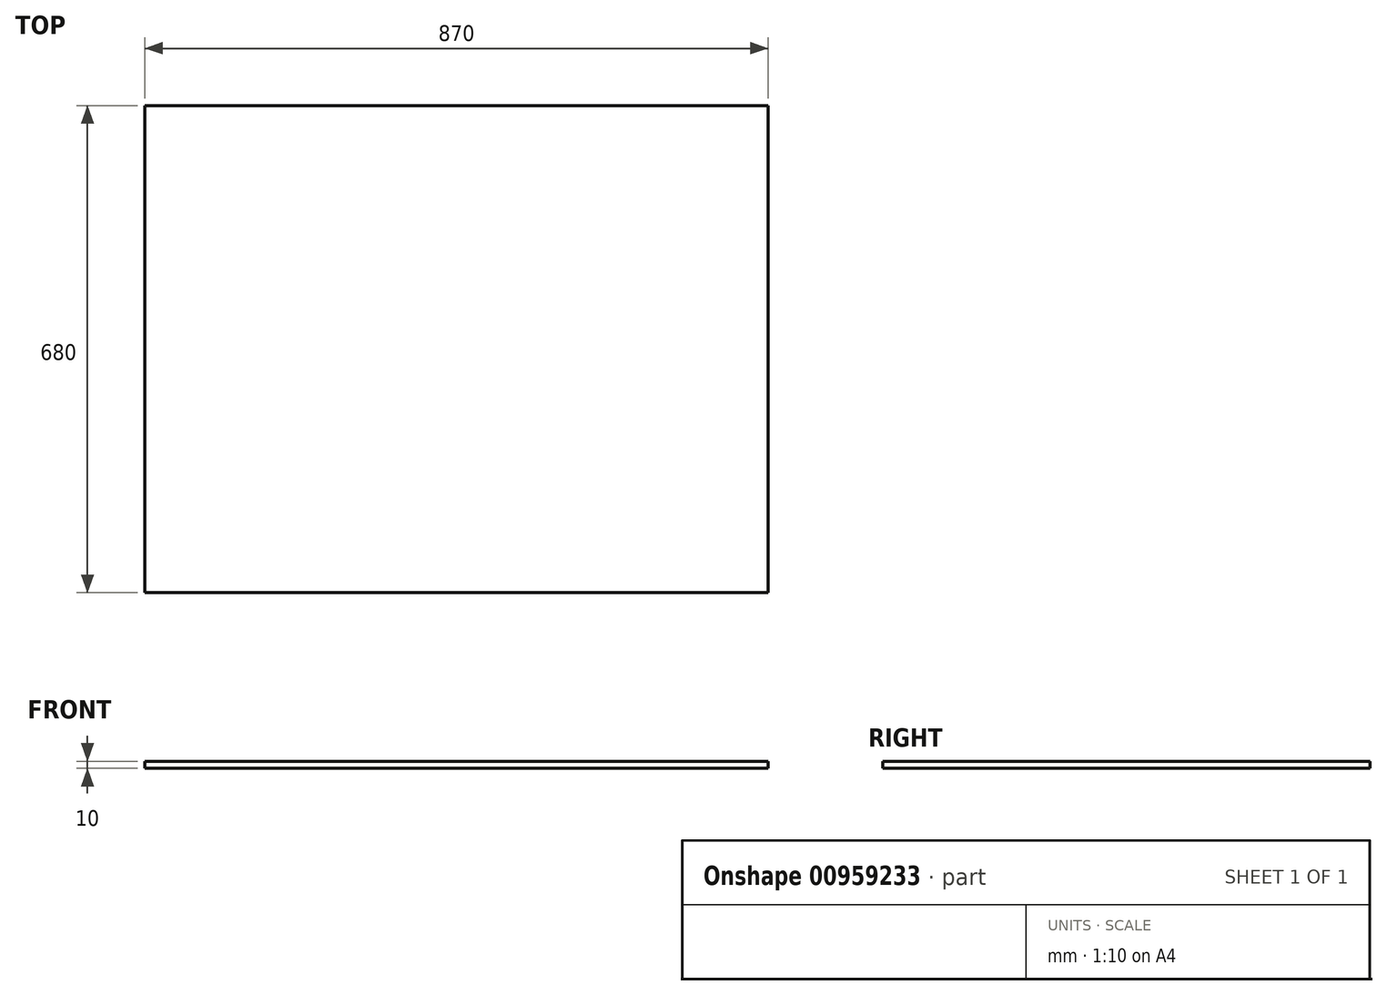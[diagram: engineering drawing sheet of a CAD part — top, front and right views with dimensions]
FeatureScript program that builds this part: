
annotation { "Feature Type Name" : "Feature", "Feature Type Description" : "" }
export const myFeature = defineFeature(function(context is Context, id is Id, definition is map)
    precondition{}
    {
        {
            var Q0;
            Q0=qCreatedBy(makeId("Top.planeOp"),FACE);
            var sketch = newSketch(context, id + "F0", { "sketchPlane" : qUnion([Q0])});
            skLineSegment(sketch, "E0.bottom", {"start": v(-434.68, -402) * mm, "end": v(435.32, -402) * mm});
            skLineSegment(sketch, "E0.top", {"start": v(-434.68, 278) * mm, "end": v(435.32, 278) * mm});
            skLineSegment(sketch, "E0.left", {"start": v(-434.68, -402) * mm, "end": v(-434.68, 278) * mm});
            skLineSegment(sketch, "E0.right", {"start": v(435.32, -402) * mm, "end": v(435.32, 278) * mm});
            skSolve(sketch);
        }
        {
            var Q0;
            Q0 = qSketchRegion(id + "F0", true);
            extrude(context, id + "F1", {"entities" : qUnion([Q0]), "depth" : 10 * mm, "offsetDistance" : 25 * mm});
        }
    });
